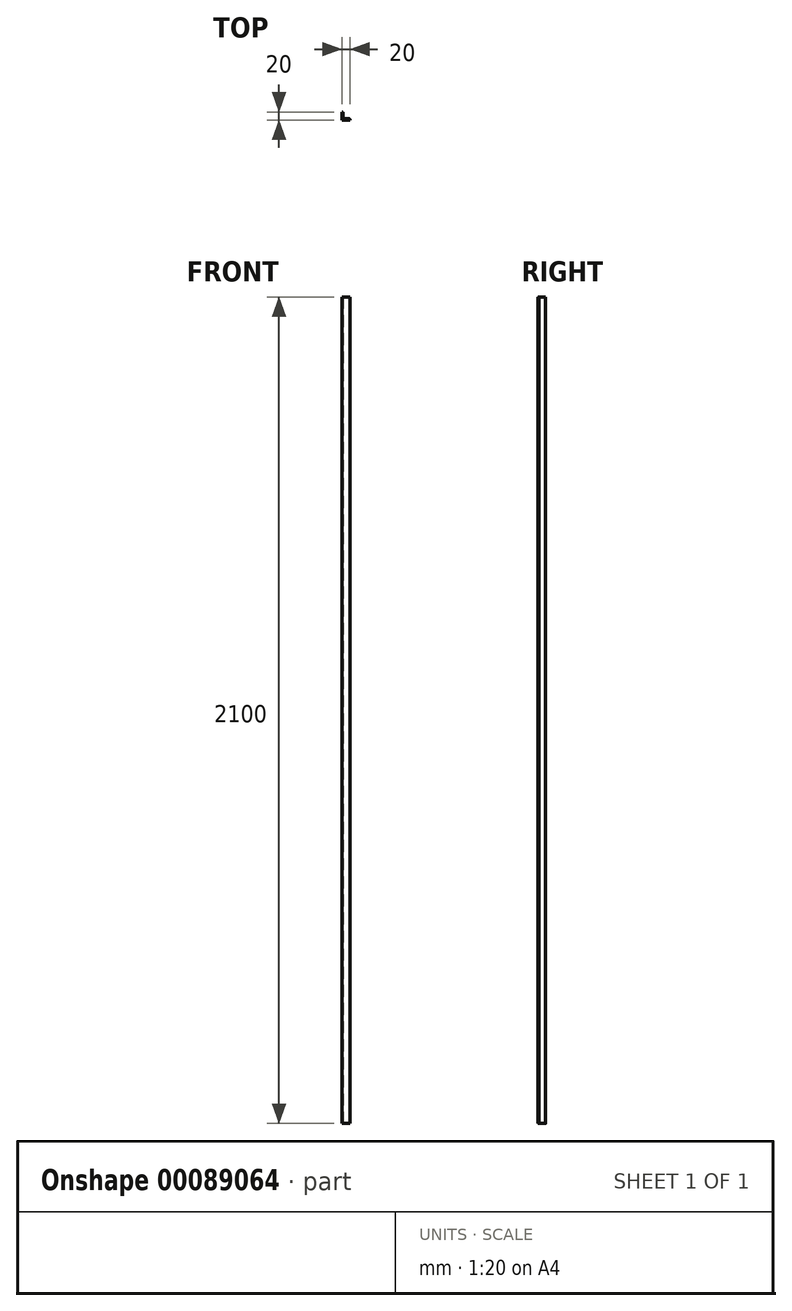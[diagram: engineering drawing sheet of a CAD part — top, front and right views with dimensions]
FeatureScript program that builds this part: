
annotation { "Feature Type Name" : "Feature", "Feature Type Description" : "" }
export const myFeature = defineFeature(function(context is Context, id is Id, definition is map)
    precondition{}
    {
        {
            var Q0;
            Q0=qCreatedBy(makeId("Top.planeOp"),FACE);
            var sketch = newSketch(context, id + "F0", { "sketchPlane" : qUnion([Q0])});
            skLineSegment(sketch, "E0", {"start": v(-10, -10) * mm, "end": v(-10, 10) * mm});
            skLineSegment(sketch, "E1", {"start": v(-10, 10) * mm, "end": v(-9, 10) * mm});
            skArc(sketch, "E2", {"start": v(-7, 8) * mm, "mid": v(-7.59, 9.41) * mm, "end": v(-9, 10) * mm});
            skLineSegment(sketch, "E3", {"start": v(-7, 8) * mm, "end": v(-7, -3.5) * mm});
            skArc(sketch, "E4", {"start": v(-7, -3.5) * mm, "mid": v(-5.97, -5.97) * mm, "end": v(-3.5, -7) * mm});
            skLineSegment(sketch, "E5", {"start": v(-3.5, -7) * mm, "end": v(8, -7) * mm});
            skArc(sketch, "E6", {"start": v(10, -9) * mm, "mid": v(9.41, -7.59) * mm, "end": v(8, -7) * mm});
            skLineSegment(sketch, "E7", {"start": v(10, -9) * mm, "end": v(10, -10) * mm});
            skLineSegment(sketch, "E8", {"start": v(10, -10) * mm, "end": v(-10, -10) * mm});
            skSolve(sketch);
        }
        {
            var Q0;
            Q0=makeQuery(id+"F0.imprint","IMPRINT",FACE,{"disambiguationData":[TD([[makeQuery(id+"F0.imprint","IMPRINT",EDGE,{"derivedFrom":sQuery(id+"F0.wireOp",EDGE,"E0")}),-1.0]])]});
            extrude(context, id + "F1", {"entities" : qUnion([Q0]), "depth" : 2100 * mm});
        }
    });
